# Revit family: Emergency_Equipment-Tepid-Floor_Mounted_Shower-S3015
name_source: partatom
category: Plumbing Fixtures
revit_build: Autodesk Revit Architecture 2016 (Build: 20150220_1215(x64)
units: mm (PartAtom-declared; Revit-internal decimal feet)

## family parameters
Always vertical = Yes
Cut with Voids When Loaded = No
OmniClass Number = 23.45.05.14.24
OmniClass Title = Eye Wash Fountains
Part Type = Normal
Room Calculation Point = No
Round Connector Dimension = Use Diameter
Shared = No
Work Plane-Based = No

## types (6) — shared parameters
CW Connection = Yes
Description = Floor Mounted Emergency Shower
Dimension Disclaimer = Dimensions are ±0.50”. Design and specifications are subject to change without notice.
HW Connection = Yes
Height = 94 "
Manufacturer = Stingray Systems
Product Documentation Link = http://www.tepid.com
Product Name = Floor Mounted Barrier Free Emergency Shower
Product Page URL = http://www.tepid.com
Shower Pull Height = 43.4 "
Supply Connection = 1"
URL = www.tepid.com
Vent Connection = No
Version = 2016-v1.0a
Waste Connection = No

## per-type parameters (varying)
| type | AB Showerhead | Base Finish | Length | Pipe Finish | SS Showerhead | Showerhead Material | Width |
| S3015-GA-NUL-NASS | No | Metal - Stingray - Epoxy Coated EP | 32.6 " | Metal - Stingray - Galvanized GA | Yes | Metal - Stingray - Stainless Steel SS | 10.4 " |
| S3015-GA-NUL-NAAB | Yes | Metal - Stingray - Epoxy Coated EP | 36.7 " | Metal - Stingray - Galvanized GA | No | Plastic - Stingray - ABS AB | 11.4 " |
| S3015-EP-NUL-NASS | No | Metal - Stingray - Epoxy Coated EP | 32.6 " | Metal - Stingray - Epoxy Coated EP | Yes | Metal - Stingray - Stainless Steel SS | 10.4 " |
| S3015-EP-NUL-NAAB | Yes | Metal - Stingray - Epoxy Coated EP | 36.7 " | Metal - Stingray - Epoxy Coated EP | No | Plastic - Stingray - ABS AB | 11.4 " |
| S3015-SS-NUL-NAAB | Yes | Metal - Stingray - Stainless Steel SS | 36.7 " | Metal - Stingray - Stainless Steel SS | No | Plastic - Stingray - ABS AB | 11.4 " |
| S3015-SS-NUL-NASS | No | Metal - Stingray - Stainless Steel SS | 32.6 " | Metal - Stingray - Stainless Steel SS | Yes | Metal - Stingray - Stainless Steel SS | 10.4 " |

note: column(s) folded — value = type name in every type: Model

## geometry (parser evidence)
native form markers: Sweep x8
no freeform markers — native parametric forms only
